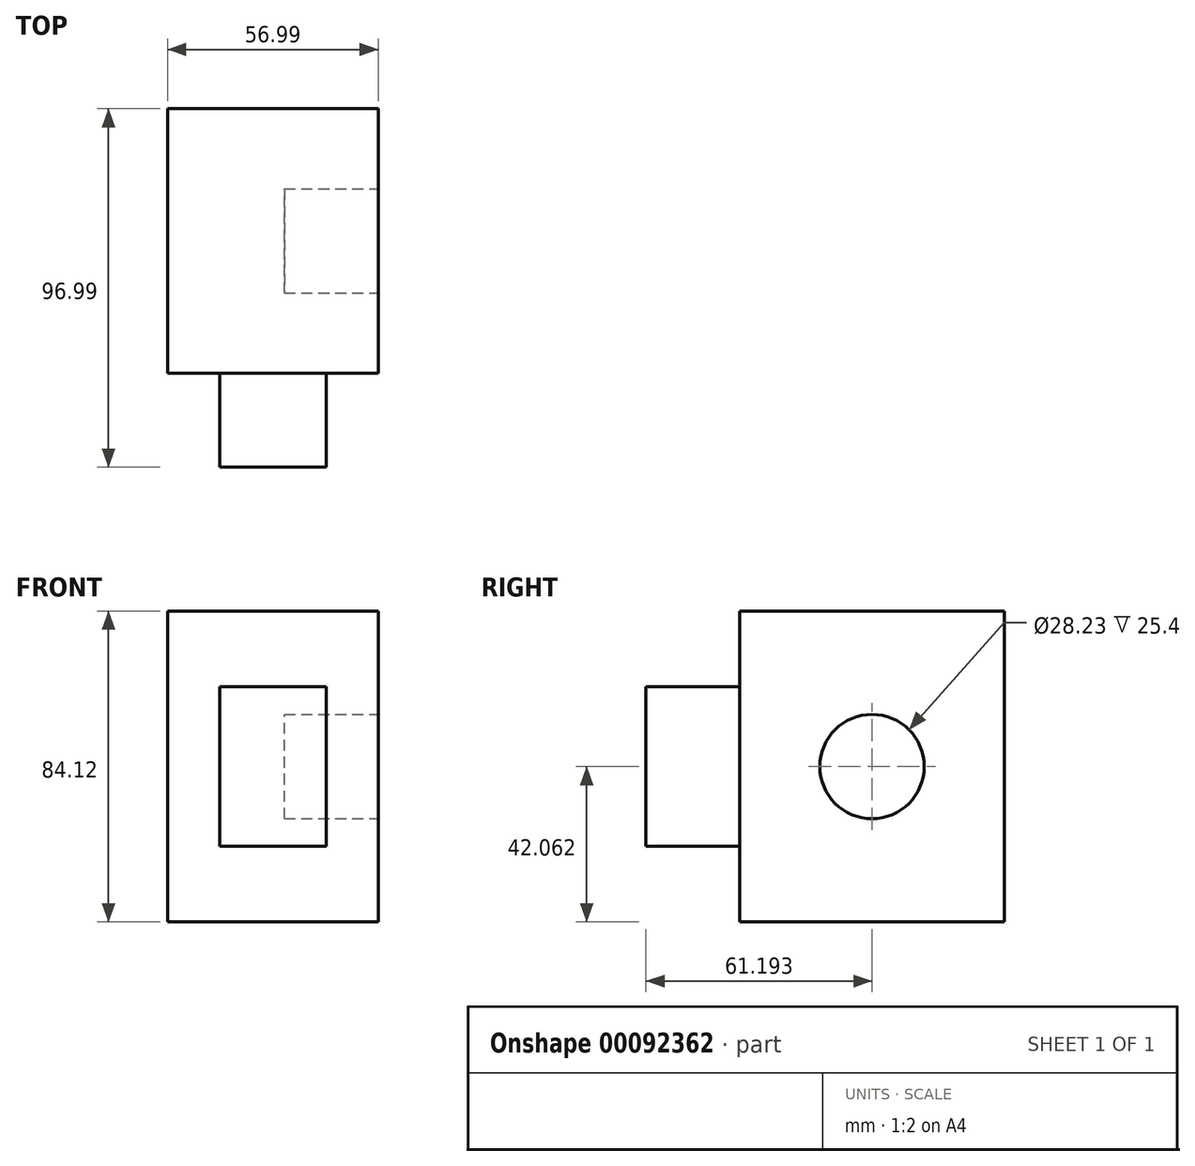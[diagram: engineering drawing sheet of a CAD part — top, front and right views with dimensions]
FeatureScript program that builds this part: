
annotation { "Feature Type Name" : "Feature", "Feature Type Description" : "" }
export const myFeature = defineFeature(function(context is Context, id is Id, definition is map)
    precondition{}
    {
        {
            var Q0;
            Q0=qCreatedBy(makeId("Front.planeOp"),FACE);
            var sketch = newSketch(context, id + "F0", { "sketchPlane" : qUnion([Q0])});
            skLineSegment(sketch, "E0.bottom", {"start": v(-112.73, 54.83) * mm, "end": v(-55.74, 54.83) * mm});
            skLineSegment(sketch, "E0.top", {"start": v(-112.73, -29.3) * mm, "end": v(-55.74, -29.3) * mm});
            skLineSegment(sketch, "E0.left", {"start": v(-112.73, 54.83) * mm, "end": v(-112.73, -29.3) * mm});
            skLineSegment(sketch, "E0.right", {"start": v(-55.74, 54.83) * mm, "end": v(-55.74, -29.3) * mm});
            skSolve(sketch);
        }
        {
            var Q0;
            Q0=makeQuery(id+"F0.imprint","IMPRINT",FACE,{"disambiguationData":[TD([[makeQuery(id+"F0.imprint","IMPRINT",EDGE,{"derivedFrom":sQuery(id+"F0.wireOp",EDGE,"E0.bottom")}),-1.0]])]});
            extrude(context, id + "F1", {"entities" : qUnion([Q0]), "depth" : 71.6 * mm});
        }
        {
            var Q0;
            Q0=makeQuery(id+"F1.opExtrude","SWEPT_FACE",FACE,{"disambiguationData":[OSD([sQuery(id+"F0.wireOp",EDGE,"E0.right")])]});
            var sketch = newSketch(context, id + "F2", { "sketchPlane" : qUnion([Q0])});
            skCircle(sketch, "E1", {"center": v(-35.8, 12.77) * mm, "radius": 14.12 * mm});
            skPoint(sketch, "E1.centerSnap0", {"position": v(-71.6, 12.77) * mm});
            skPoint(sketch, "E1.centerSnap1", {"position": v(-35.8, -29.3) * mm});
            skSolve(sketch);
        }
        {
            var Q0;
            Q0=makeQuery(id+"F2.imprint","IMPRINT",FACE,{"disambiguationData":[TD([[makeQuery(id+"F2.imprint","IMPRINT",EDGE,{"derivedFrom":sQuery(id+"F2.wireOp",EDGE,"E1")}),1.0]])]});
            extrude(context, id + "F3", {"entities" : qUnion([Q0]), "operationType" : NewBodyOperationType.REMOVE, "oppositeDirection" : true, "depth" : 25.4 * mm});
        }
        {
            var Q0;
            Q0=makeQuery(id+"F1.opExtrude","CAP_FACE",FACE,{"disambiguationData":[OSD([sQuery(id+"F0.wireOp",EDGE,"E0.bottom"),sQuery(id+"F0.wireOp",EDGE,"E0.top"),sQuery(id+"F0.wireOp",EDGE,"E0.left"),sQuery(id+"F0.wireOp",EDGE,"E0.right")])],"isStart":false});
            var sketch = newSketch(context, id + "F4", { "sketchPlane" : qUnion([Q0])});
            skLineSegment(sketch, "E2.bottom", {"start": v(-98.63, 34.37) * mm, "end": v(-69.83, 34.37) * mm});
            skLineSegment(sketch, "E2.top", {"start": v(-98.63, -8.83) * mm, "end": v(-69.83, -8.83) * mm});
            skLineSegment(sketch, "E2.left", {"start": v(-98.63, 34.37) * mm, "end": v(-98.63, -8.83) * mm});
            skLineSegment(sketch, "E2.right", {"start": v(-69.83, 34.37) * mm, "end": v(-69.83, -8.83) * mm});
            skPoint(sketch, "E2.middle", {"position": v(-84.23, 12.77) * mm});
            skPoint(sketch, "E2.middle.positionSnap0", {"position": v(-84.23, -29.3) * mm});
            skPoint(sketch, "E2.middle.positionSnap1", {"position": v(-55.74, 12.77) * mm});
            skPoint(sketch, "E2.centerSnap0", {"position": v(-84.23, -29.3) * mm});
            skPoint(sketch, "E2.centerSnap1", {"position": v(-55.74, 12.77) * mm});
            skSolve(sketch);
        }
        {
            var Q0;
            Q0=makeQuery(id+"F4.imprint","IMPRINT",FACE,{"disambiguationData":[TD([[makeQuery(id+"F4.imprint","IMPRINT",EDGE,{"derivedFrom":sQuery(id+"F4.wireOp",EDGE,"E2.bottom")}),-1.0]])]});
            extrude(context, id + "F5", {"entities" : qUnion([Q0]), "operationType" : NewBodyOperationType.ADD, "depth" : 25.4 * mm});
        }
    });
